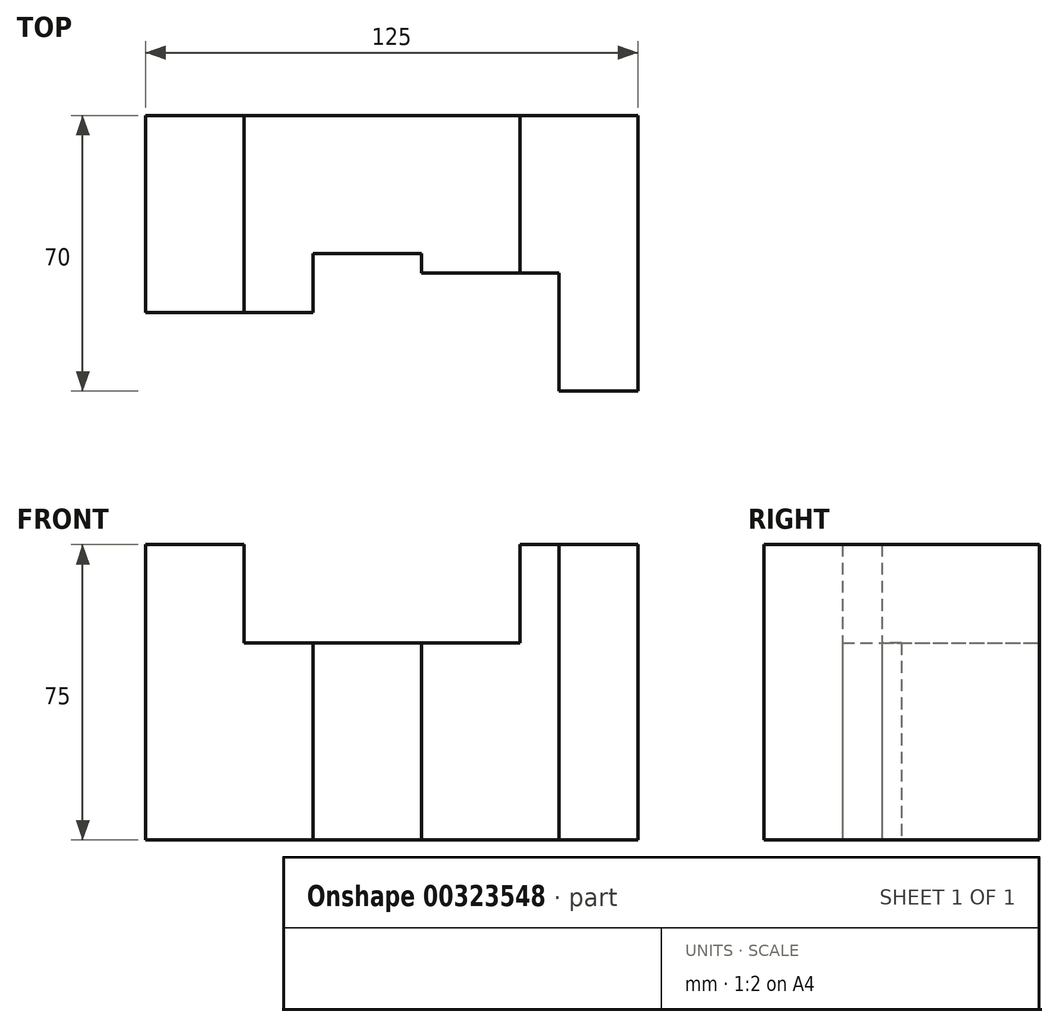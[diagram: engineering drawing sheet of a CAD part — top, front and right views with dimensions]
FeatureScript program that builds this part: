
annotation { "Feature Type Name" : "Feature", "Feature Type Description" : "" }
export const myFeature = defineFeature(function(context is Context, id is Id, definition is map)
    precondition{}
    {
        {
            var Q0;
            Q0=qCreatedBy(makeId("Top.planeOp"),FACE);
            var sketch = newSketch(context, id + "F0", { "sketchPlane" : qUnion([Q0])});
            skLineSegment(sketch, "E0", {"start": v(0, 0) * mm, "end": v(0, 50) * mm});
            skLineSegment(sketch, "E1", {"start": v(0, 50) * mm, "end": v(25, 50) * mm});
            skLineSegment(sketch, "E2", {"start": v(25, 50) * mm, "end": v(25, 0) * mm, "construction": true});
            skLineSegment(sketch, "E3", {"start": v(0, 0) * mm, "end": v(25, 0) * mm});
            skLineSegment(sketch, "E4", {"start": v(25, 0) * mm, "end": v(42.5, 0) * mm});
            skLineSegment(sketch, "E5", {"start": v(42.5, 0) * mm, "end": v(42.5, 15) * mm});
            skLineSegment(sketch, "E6", {"start": v(42.5, 15) * mm, "end": v(45, 15) * mm});
            skLineSegment(sketch, "E7", {"start": v(45, 15) * mm, "end": v(70, 15) * mm});
            skLineSegment(sketch, "E8", {"start": v(70, 15) * mm, "end": v(70, 10) * mm});
            skLineSegment(sketch, "E9", {"start": v(70, 10) * mm, "end": v(105, 10) * mm});
            skLineSegment(sketch, "E10", {"start": v(105, 10) * mm, "end": v(105, -20) * mm});
            skLineSegment(sketch, "E11", {"start": v(105, -20) * mm, "end": v(125, -20) * mm});
            skLineSegment(sketch, "E12", {"start": v(125, -20) * mm, "end": v(125, 50) * mm});
            skPoint(sketch, "E12.endSnap0", {"position": v(12.5, 50) * mm});
            skLineSegment(sketch, "E13", {"start": v(125, 50) * mm, "end": v(25, 50) * mm});
            skSolve(sketch);
        }
        {
            var Q0;
            Q0 = qSketchRegion(id + "F0", true);
            extrude(context, id + "F1", {"entities" : qUnion([Q0]), "depth" : 50 * mm});
        }
        {
            var Q0;
            Q0=makeQuery(id+"F1.opExtrude","CAP_FACE",FACE,{"disambiguationData":[OSD([sQuery(id+"F0.wireOp",EDGE,"E0"),sQuery(id+"F0.wireOp",EDGE,"E1"),sQuery(id+"F0.wireOp",EDGE,"E3"),sQuery(id+"F0.wireOp",EDGE,"E4"),sQuery(id+"F0.wireOp",EDGE,"E5"),sQuery(id+"F0.wireOp",EDGE,"E6"),sQuery(id+"F0.wireOp",EDGE,"E7"),sQuery(id+"F0.wireOp",EDGE,"E8"),sQuery(id+"F0.wireOp",EDGE,"E9"),sQuery(id+"F0.wireOp",EDGE,"E10"),sQuery(id+"F0.wireOp",EDGE,"E11"),sQuery(id+"F0.wireOp",EDGE,"E12"),sQuery(id+"F0.wireOp",EDGE,"E13")])],"isStart":false});
            var sketch = newSketch(context, id + "F2", { "sketchPlane" : qUnion([Q0])});
            skLineSegment(sketch, "E14", {"start": v(0, 0) * mm, "end": v(25, 0) * mm});
            skLineSegment(sketch, "E15", {"start": v(25, 0) * mm, "end": v(25, 50) * mm});
            skLineSegment(sketch, "E16", {"start": v(25, 50) * mm, "end": v(0, 50) * mm});
            skLineSegment(sketch, "E17", {"start": v(0, 50) * mm, "end": v(0, 0) * mm});
            skLineSegment(sketch, "E18", {"start": v(125, 50) * mm, "end": v(125, -20) * mm});
            skLineSegment(sketch, "E19", {"start": v(125, -20) * mm, "end": v(105, -20) * mm});
            skLineSegment(sketch, "E20", {"start": v(105, -20) * mm, "end": v(105, 10) * mm});
            skLineSegment(sketch, "E21", {"start": v(105, 10) * mm, "end": v(95, 10) * mm});
            skLineSegment(sketch, "E22", {"start": v(95, 10) * mm, "end": v(95, 50) * mm});
            skLineSegment(sketch, "E23", {"start": v(95, 50) * mm, "end": v(125, 50) * mm});
            skSolve(sketch);
        }
        {
            var Q0;
            Q0 = qSketchRegion(id + "F2", true);
            extrude(context, id + "F3", {"entities" : qUnion([Q0]), "operationType" : NewBodyOperationType.ADD, "depth" : 25 * mm});
        }
    });
